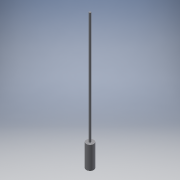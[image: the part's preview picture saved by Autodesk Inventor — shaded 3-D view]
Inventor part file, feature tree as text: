
AUTODESK INVENTOR PART (.ipt)
format: ipt  version: 2016 (Build 200138000, 138)  size: 93,184 bytes
history: native  units: in
note: dims shown in document units (in); Inventor stores cm internally (conversion verified against a paired STEP export)
features: sketch x3, extrude x2
ambient origin geometry x8: Origin, YZ Plane, XZ Plane, XY Plane, X Axis, Y Axis, Z Axis, Center Point
bodies: Solid1 (feature_tree)
feature tree (5):
  extrude  "Extrusion1"  Depth=3.0in TaperAngle=0.0deg
  extrude  "Extrusion2"  Depth=18.5in TaperAngle=0.0deg
  sketch  "Sketch3"
  sketch  "Sketch1"  dims[d0=1.0in d1=3.0in d2=0.0in]
  sketch  "Sketch2"  dims[d3=0.25in d4=18.5in d5=0.0in]
